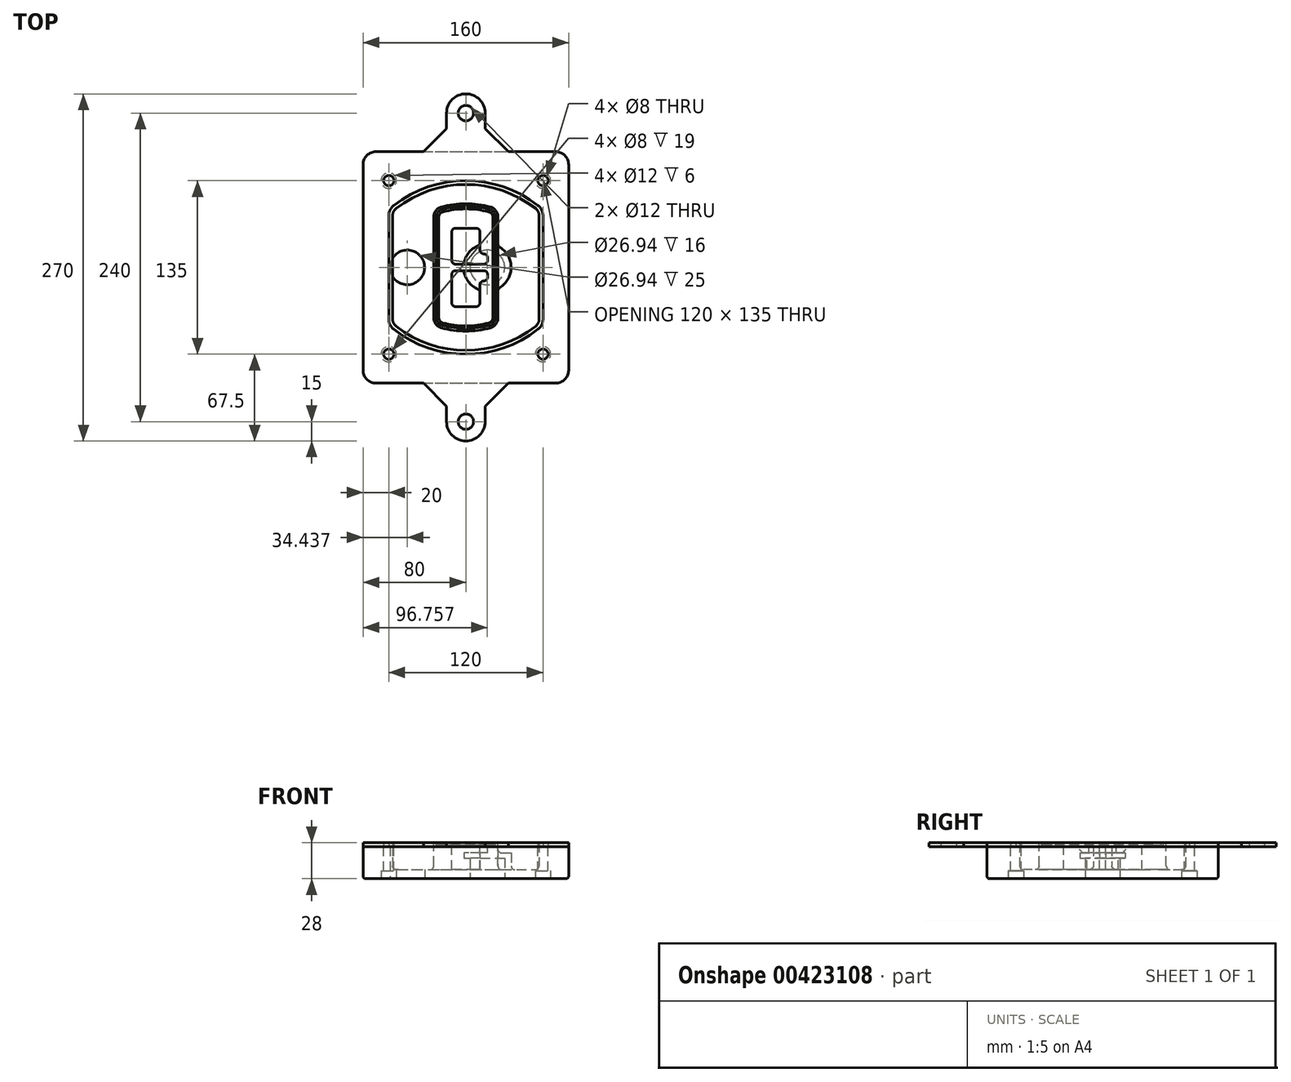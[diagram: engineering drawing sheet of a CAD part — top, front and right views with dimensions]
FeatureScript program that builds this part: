
annotation { "Feature Type Name" : "Feature", "Feature Type Description" : "" }
export const myFeature = defineFeature(function(context is Context, id is Id, definition is map)
    precondition{}
    {
        {
            var Q0;
            Q0=qCreatedBy(makeId("Top.planeOp"),FACE);
            var sketch = newSketch(context, id + "F0", { "sketchPlane" : qUnion([Q0])});
            skPoint(sketch, "E0.rect.middle", {"position": v(0, 0) * mm});
            skLineSegment(sketch, "E1.bottom", {"start": v(-70, -90) * mm, "end": v(70, -90) * mm});
            skLineSegment(sketch, "E1.top", {"start": v(-70, 90) * mm, "end": v(70, 90) * mm});
            skLineSegment(sketch, "E1.left", {"start": v(-80, -80) * mm, "end": v(-80, 80) * mm});
            skLineSegment(sketch, "E1.right", {"start": v(80, -80) * mm, "end": v(80, 80) * mm});
            skLineSegment(sketch, "E2", {"start": v(-80, 90) * mm, "end": v(80, -90) * mm, "construction": true});
            skLineSegment(sketch, "E3", {"start": v(80, 90) * mm, "end": v(-80, -90) * mm, "construction": true});
            skCircle(sketch, "E4", {"center": v(-60, 67.5) * mm, "radius": 4 * mm});
            skCircle(sketch, "E5", {"center": v(60, 67.5) * mm, "radius": 4 * mm});
            skCircle(sketch, "E6", {"center": v(60, -67.5) * mm, "radius": 4 * mm});
            skCircle(sketch, "E7", {"center": v(-60, -67.5) * mm, "radius": 4 * mm});
            skLineSegment(sketch, "E8", {"start": v(-60, 67.5) * mm, "end": v(60, 67.5) * mm, "construction": true});
            skLineSegment(sketch, "E9", {"start": v(60, 67.5) * mm, "end": v(60, -67.5) * mm, "construction": true});
            skLineSegment(sketch, "E10", {"start": v(60, -67.5) * mm, "end": v(-60, -67.5) * mm, "construction": true});
            skLineSegment(sketch, "E11", {"start": v(-60, -67.5) * mm, "end": v(-60, 67.5) * mm, "construction": true});
            skLineSegment(sketch, "E12", {"start": v(-60, 40.3) * mm, "end": v(-60, -40.3) * mm});
            skLineSegment(sketch, "E13", {"start": v(60, 40.3) * mm, "end": v(60, -40.3) * mm});
            skArc(sketch, "E14", {"start": v(56.15, 48.18) * mm, "mid": v(0, 67.5) * mm, "end": v(-56.15, 48.18) * mm});
            skArc(sketch, "E15", {"start": v(-56.15, -48.18) * mm, "mid": v(0, -67.5) * mm, "end": v(56.15, -48.18) * mm});
            skLineSegment(sketch, "E16", {"start": v(-60, 0) * mm, "end": v(60, 0) * mm, "construction": true});
            skPoint(sketch, "E17.visualSharp", {"position": v(-60, -45) * mm});
            skArc(sketch, "E17.filletArc", {"start": v(-60, -40.3) * mm, "mid": v(-58.99, -44.68) * mm, "end": v(-56.15, -48.18) * mm});
            skPoint(sketch, "E18.visualSharp", {"position": v(-60, 45) * mm});
            skArc(sketch, "E18.filletArc", {"start": v(-56.15, 48.18) * mm, "mid": v(-58.99, 44.68) * mm, "end": v(-60, 40.3) * mm});
            skPoint(sketch, "E19.visualSharp", {"position": v(60, 45) * mm});
            skArc(sketch, "E19.filletArc", {"start": v(60, 40.3) * mm, "mid": v(58.99, 44.68) * mm, "end": v(56.15, 48.18) * mm});
            skPoint(sketch, "E20.visualSharp", {"position": v(60, -45) * mm});
            skArc(sketch, "E20.filletArc", {"start": v(56.15, -48.18) * mm, "mid": v(58.99, -44.68) * mm, "end": v(60, -40.3) * mm});
            skPoint(sketch, "E21.visualSharp", {"position": v(-80, 90) * mm});
            skArc(sketch, "E21.filletArc", {"start": v(-70, 90) * mm, "mid": v(-77.07, 87.07) * mm, "end": v(-80, 80) * mm});
            skPoint(sketch, "E22.visualSharp", {"position": v(80, 90) * mm});
            skArc(sketch, "E22.filletArc", {"start": v(80, 80) * mm, "mid": v(77.07, 87.07) * mm, "end": v(70, 90) * mm});
            skPoint(sketch, "E23.visualSharp", {"position": v(80, -90) * mm});
            skArc(sketch, "E23.filletArc", {"start": v(70, -90) * mm, "mid": v(77.07, -87.07) * mm, "end": v(80, -80) * mm});
            skPoint(sketch, "E24.visualSharp", {"position": v(-80, -90) * mm});
            skArc(sketch, "E24.filletArc", {"start": v(-80, -80) * mm, "mid": v(-77.07, -87.07) * mm, "end": v(-70, -90) * mm});
            skArc(sketch, "E25.0", {"start": v(57, 40.3) * mm, "mid": v(56.3, 43.36) * mm, "end": v(54.3, 45.81) * mm});
            skLineSegment(sketch, "E25.1", {"start": v(57, 40.3) * mm, "end": v(57, -40.3) * mm});
            skArc(sketch, "E25.2", {"start": v(54.3, -45.81) * mm, "mid": v(56.3, -43.36) * mm, "end": v(57, -40.3) * mm});
            skArc(sketch, "E25.3", {"start": v(-54.3, -45.81) * mm, "mid": v(0, -64.5) * mm, "end": v(54.3, -45.81) * mm});
            skArc(sketch, "E25.4", {"start": v(-57, -40.3) * mm, "mid": v(-56.3, -43.36) * mm, "end": v(-54.3, -45.81) * mm});
            skArc(sketch, "E25.5", {"start": v(54.3, 45.81) * mm, "mid": v(0, 64.5) * mm, "end": v(-54.3, 45.81) * mm});
            skLineSegment(sketch, "E25.6", {"start": v(-57, 40.3) * mm, "end": v(-57, -40.3) * mm});
            skArc(sketch, "E25.7", {"start": v(-54.3, 45.81) * mm, "mid": v(-56.3, 43.36) * mm, "end": v(-57, 40.3) * mm});
            skArc(sketch, "E26.0", {"start": v(-58.62, 51.33) * mm, "mid": v(-62.58, 46.43) * mm, "end": v(-64, 40.3) * mm});
            skArc(sketch, "E26.1", {"start": v(58.62, 51.33) * mm, "mid": v(0, 71.5) * mm, "end": v(-58.62, 51.33) * mm});
            skArc(sketch, "E26.2", {"start": v(64, 40.3) * mm, "mid": v(62.58, 46.43) * mm, "end": v(58.62, 51.33) * mm});
            skLineSegment(sketch, "E26.3", {"start": v(64, 40.3) * mm, "end": v(64, -40.3) * mm});
            skArc(sketch, "E26.4", {"start": v(58.62, -51.33) * mm, "mid": v(62.58, -46.43) * mm, "end": v(64, -40.3) * mm});
            skLineSegment(sketch, "E26.5", {"start": v(-64, 40.3) * mm, "end": v(-64, -40.3) * mm});
            skArc(sketch, "E26.6", {"start": v(-58.62, -51.33) * mm, "mid": v(0, -71.5) * mm, "end": v(58.62, -51.33) * mm});
            skArc(sketch, "E26.7", {"start": v(-64, -40.3) * mm, "mid": v(-62.58, -46.43) * mm, "end": v(-58.62, -51.33) * mm});
            skSolve(sketch);
        }
        {
            var Q0;
            Q0=makeQuery(id+"F0.imprint","IMPRINT",FACE,{"disambiguationData":[TD([[makeQuery(id+"F0.imprint","IMPRINT",EDGE,{"derivedFrom":sQuery(id+"F0.wireOp",EDGE,"E1.bottom")}),1.0]])]});
            var Q1;
            Q1=makeQuery(id+"F0.imprint","IMPRINT",FACE,{"disambiguationData":[TD([[makeQuery(id+"F0.imprint","IMPRINT",EDGE,{"derivedFrom":sQuery(id+"F0.wireOp",EDGE,"E12")}),1.0]])]});
            var Q2;
            Q2=makeQuery(id+"F0.imprint","IMPRINT",FACE,{"disambiguationData":[TD([[makeQuery(id+"F0.imprint","IMPRINT",EDGE,{"derivedFrom":sQuery(id+"F0.wireOp",EDGE,"E25.0")}),1.0]])]});
            var Q3;
            Q3=makeQuery(id+"F0.imprint","IMPRINT",FACE,{"disambiguationData":[TD([[makeQuery(id+"F0.imprint","IMPRINT",EDGE,{"derivedFrom":sQuery(id+"F0.wireOp",EDGE,"E12")}),-1.0]])]});
            extrude(context, id + "F1", {"entities" : qUnion([Q0, Q1, Q2, Q3]), "oppositeDirection" : true, "depth" : 25 * mm});
        }
        {
            var Q0;
            Q0=makeQuery(id+"F0.imprint","IMPRINT",FACE,{"disambiguationData":[TD([[makeQuery(id+"F0.imprint","IMPRINT",EDGE,{"derivedFrom":sQuery(id+"F0.wireOp",EDGE,"E12")}),1.0]])]});
            extrude(context, id + "F2", {"entities" : qUnion([Q0]), "operationType" : NewBodyOperationType.ADD, "depth" : 3 * mm});
        }
        {
            var Q0;
            Q0=makeQuery(id+"F0.imprint","IMPRINT",FACE,{"disambiguationData":[TD([[makeQuery(id+"F0.imprint","IMPRINT",EDGE,{"derivedFrom":sQuery(id+"F0.wireOp",EDGE,"E25.0")}),1.0]])]});
            extrude(context, id + "F3", {"entities" : qUnion([Q0]), "operationType" : NewBodyOperationType.REMOVE, "oppositeDirection" : true, "depth" : 18 * mm});
        }
        {
            var Q0;
            Q0=makeQuery(id+"F2.opExtrude","CAP_FACE",FACE,{"disambiguationData":[OSD([sQuery(id+"F0.wireOp",EDGE,"E12"),sQuery(id+"F0.wireOp",EDGE,"E13"),sQuery(id+"F0.wireOp",EDGE,"E14"),sQuery(id+"F0.wireOp",EDGE,"E15"),sQuery(id+"F0.wireOp",EDGE,"E17.filletArc"),sQuery(id+"F0.wireOp",EDGE,"E18.filletArc"),sQuery(id+"F0.wireOp",EDGE,"E19.filletArc"),sQuery(id+"F0.wireOp",EDGE,"E20.filletArc"),sQuery(id+"F0.wireOp",EDGE,"E25.0"),sQuery(id+"F0.wireOp",EDGE,"E25.1"),sQuery(id+"F0.wireOp",EDGE,"E25.2"),sQuery(id+"F0.wireOp",EDGE,"E25.3"),sQuery(id+"F0.wireOp",EDGE,"E25.4"),sQuery(id+"F0.wireOp",EDGE,"E25.5"),sQuery(id+"F0.wireOp",EDGE,"E25.6"),sQuery(id+"F0.wireOp",EDGE,"E25.7")])],"isStart":false});
            var sketch = newSketch(context, id + "F4", { "sketchPlane" : qUnion([Q0])});
            skArc(sketch, "E27.0", {"start": v(-19.08, -46.97) * mm, "mid": v(0, -49.5) * mm, "end": v(19.08, -46.97) * mm});
            skArc(sketch, "E28.0", {"start": v(19.08, 46.97) * mm, "mid": v(0, 49.5) * mm, "end": v(-19.08, 46.97) * mm});
            skLineSegment(sketch, "E29", {"start": v(-25, 39.25) * mm, "end": v(-25, -39.25) * mm});
            skLineSegment(sketch, "E30", {"start": v(25, 39.25) * mm, "end": v(25, -39.25) * mm});
            skLineSegment(sketch, "E31", {"start": v(-25, 45.1) * mm, "end": v(25, 45.1) * mm, "construction": true});
            skLineSegment(sketch, "E32", {"start": v(-25, -45.1) * mm, "end": v(25, -45.1) * mm, "construction": true});
            skPoint(sketch, "E33.visualSharp", {"position": v(-25, 45.1) * mm});
            skArc(sketch, "E33.filletArc", {"start": v(-19.08, 46.97) * mm, "mid": v(-23.35, 44.11) * mm, "end": v(-25, 39.25) * mm});
            skPoint(sketch, "E34.visualSharp", {"position": v(25, 45.1) * mm});
            skArc(sketch, "E34.filletArc", {"start": v(25, 39.25) * mm, "mid": v(23.35, 44.11) * mm, "end": v(19.08, 46.97) * mm});
            skPoint(sketch, "E35.visualSharp", {"position": v(25, -45.1) * mm});
            skArc(sketch, "E35.filletArc", {"start": v(19.08, -46.97) * mm, "mid": v(23.35, -44.11) * mm, "end": v(25, -39.25) * mm});
            skPoint(sketch, "E36.visualSharp", {"position": v(-25, -45.1) * mm});
            skArc(sketch, "E36.filletArc", {"start": v(-25, -39.25) * mm, "mid": v(-23.35, -44.11) * mm, "end": v(-19.08, -46.97) * mm});
            skArc(sketch, "E37.0", {"start": v(54.3, 45.81) * mm, "mid": v(0, 64.5) * mm, "end": v(-54.3, 45.81) * mm});
            skArc(sketch, "E37.1", {"start": v(-54.3, 45.81) * mm, "mid": v(-56.3, 43.36) * mm, "end": v(-57, 40.3) * mm});
            skLineSegment(sketch, "E37.2", {"start": v(-57, 40.3) * mm, "end": v(-57, -40.3) * mm});
            skArc(sketch, "E37.3", {"start": v(-57, -40.3) * mm, "mid": v(-56.3, -43.36) * mm, "end": v(-54.3, -45.81) * mm});
            skArc(sketch, "E37.4", {"start": v(-54.3, -45.81) * mm, "mid": v(0, -64.5) * mm, "end": v(54.3, -45.81) * mm});
            skArc(sketch, "E37.5", {"start": v(54.3, -45.81) * mm, "mid": v(56.3, -43.36) * mm, "end": v(57, -40.3) * mm});
            skLineSegment(sketch, "E37.6", {"start": v(57, 40.3) * mm, "end": v(57, -40.3) * mm});
            skArc(sketch, "E37.7", {"start": v(57, 40.3) * mm, "mid": v(56.3, 43.36) * mm, "end": v(54.3, 45.81) * mm});
            skLineSegment(sketch, "E38.0", {"start": v(23, 39.25) * mm, "end": v(23, -39.25) * mm});
            skArc(sketch, "E38.1", {"start": v(18.56, -45.04) * mm, "mid": v(21.76, -42.9) * mm, "end": v(23, -39.25) * mm});
            skArc(sketch, "E38.2", {"start": v(-18.56, -45.04) * mm, "mid": v(0, -47.5) * mm, "end": v(18.56, -45.04) * mm});
            skArc(sketch, "E38.3", {"start": v(-23, -39.25) * mm, "mid": v(-21.76, -42.9) * mm, "end": v(-18.56, -45.04) * mm});
            skLineSegment(sketch, "E38.4", {"start": v(-23, 39.25) * mm, "end": v(-23, -39.25) * mm});
            skArc(sketch, "E38.5", {"start": v(23, 39.25) * mm, "mid": v(21.76, 42.9) * mm, "end": v(18.56, 45.04) * mm});
            skArc(sketch, "E38.6", {"start": v(-18.56, 45.04) * mm, "mid": v(-21.76, 42.9) * mm, "end": v(-23, 39.25) * mm});
            skArc(sketch, "E38.7", {"start": v(18.56, 45.04) * mm, "mid": v(0, 47.5) * mm, "end": v(-18.56, 45.04) * mm});
            skArc(sketch, "E39.0", {"start": v(21, 39.25) * mm, "mid": v(20.18, 41.68) * mm, "end": v(18.04, 43.1) * mm});
            skLineSegment(sketch, "E39.1", {"start": v(21, 39.25) * mm, "end": v(21, -39.25) * mm});
            skArc(sketch, "E39.2", {"start": v(18.04, -43.1) * mm, "mid": v(20.18, -41.68) * mm, "end": v(21, -39.25) * mm});
            skArc(sketch, "E39.3", {"start": v(-18.04, -43.1) * mm, "mid": v(0, -45.5) * mm, "end": v(18.04, -43.1) * mm});
            skArc(sketch, "E39.4", {"start": v(-21, -39.25) * mm, "mid": v(-20.18, -41.68) * mm, "end": v(-18.04, -43.1) * mm});
            skArc(sketch, "E39.5", {"start": v(18.04, 43.1) * mm, "mid": v(0, 45.5) * mm, "end": v(-18.04, 43.1) * mm});
            skLineSegment(sketch, "E39.6", {"start": v(-21, 39.25) * mm, "end": v(-21, -39.25) * mm});
            skArc(sketch, "E39.7", {"start": v(-18.04, 43.1) * mm, "mid": v(-20.18, 41.68) * mm, "end": v(-21, 39.25) * mm});
            skLineSegment(sketch, "E40", {"start": v(-25, 0) * mm, "end": v(25, 0) * mm, "construction": true});
            skLineSegment(sketch, "E41", {"start": v(-11, 5.5) * mm, "end": v(-11, 27.5) * mm});
            skLineSegment(sketch, "E42", {"start": v(-8, 30.5) * mm, "end": v(8, 30.5) * mm});
            skLineSegment(sketch, "E43", {"start": v(11, 27.5) * mm, "end": v(11, 13.5) * mm});
            skLineSegment(sketch, "E44", {"start": v(14, 10.5) * mm, "end": v(14, 10.5) * mm});
            skLineSegment(sketch, "E45", {"start": v(17, 7.5) * mm, "end": v(17, 5.5) * mm});
            skLineSegment(sketch, "E46", {"start": v(14, 2.5) * mm, "end": v(-8, 2.5) * mm});
            skPoint(sketch, "E47.visualSharp", {"position": v(-11, 30.5) * mm});
            skArc(sketch, "E47.filletArc", {"start": v(-8, 30.5) * mm, "mid": v(-10.12, 29.62) * mm, "end": v(-11, 27.5) * mm});
            skPoint(sketch, "E48.visualSharp", {"position": v(11, 30.5) * mm});
            skArc(sketch, "E48.filletArc", {"start": v(11, 27.5) * mm, "mid": v(10.12, 29.62) * mm, "end": v(8, 30.5) * mm});
            skPoint(sketch, "E49.visualSharp", {"position": v(11, 10.5) * mm});
            skArc(sketch, "E49.filletArc", {"start": v(11, 13.5) * mm, "mid": v(11.88, 11.38) * mm, "end": v(14, 10.5) * mm});
            skPoint(sketch, "E50.visualSharp", {"position": v(17, 10.5) * mm});
            skArc(sketch, "E50.filletArc", {"start": v(17, 7.5) * mm, "mid": v(16.12, 9.62) * mm, "end": v(14, 10.5) * mm});
            skPoint(sketch, "E51.visualSharp", {"position": v(17, 2.5) * mm});
            skArc(sketch, "E51.filletArc", {"start": v(14, 2.5) * mm, "mid": v(16.12, 3.38) * mm, "end": v(17, 5.5) * mm});
            skPoint(sketch, "E52.visualSharp", {"position": v(-11, 2.5) * mm});
            skArc(sketch, "E52.filletArc", {"start": v(-11, 5.5) * mm, "mid": v(-10.12, 3.38) * mm, "end": v(-8, 2.5) * mm});
            skLineSegment(sketch, "E53.0.MirrorCS", {"start": v(14, -2.5) * mm, "end": v(-8, -2.5) * mm});
            skArc(sketch, "E54.0.MirrorCS", {"start": v(-11, -5.5) * mm, "mid": v(-10.12, -3.38) * mm, "end": v(-8, -2.5) * mm});
            skLineSegment(sketch, "E55.0.MirrorCS", {"start": v(-11, -5.5) * mm, "end": v(-11, -27.5) * mm});
            skArc(sketch, "E56.0.MirrorCS", {"start": v(-8, -30.5) * mm, "mid": v(-10.12, -29.62) * mm, "end": v(-11, -27.5) * mm});
            skLineSegment(sketch, "E57.0.MirrorCS", {"start": v(-8, -30.5) * mm, "end": v(8, -30.5) * mm});
            skArc(sketch, "E58.0.MirrorCS", {"start": v(11, -27.5) * mm, "mid": v(10.12, -29.62) * mm, "end": v(8, -30.5) * mm});
            skLineSegment(sketch, "E59.0.MirrorCS", {"start": v(11, -27.5) * mm, "end": v(11, -13.5) * mm});
            skArc(sketch, "E60.0.MirrorCS", {"start": v(11, -13.5) * mm, "mid": v(11.88, -11.38) * mm, "end": v(14, -10.5) * mm});
            skArc(sketch, "E61.0.MirrorCS", {"start": v(17, -7.5) * mm, "mid": v(16.12, -9.62) * mm, "end": v(14, -10.5) * mm});
            skLineSegment(sketch, "E62.0.MirrorCS", {"start": v(17, -7.5) * mm, "end": v(17, -5.5) * mm});
            skArc(sketch, "E63.0.MirrorCS", {"start": v(14, -2.5) * mm, "mid": v(16.12, -3.38) * mm, "end": v(17, -5.5) * mm});
            skSolve(sketch);
        }
        {
            var Q0;
            Q0=makeQuery(id+"F4.imprint","IMPRINT",FACE,{"disambiguationData":[TD([[makeQuery(id+"F4.imprint","IMPRINT",EDGE,{"derivedFrom":sQuery(id+"F4.wireOp",EDGE,"E27.0")}),1.0]])]});
            var Q1;
            Q1=makeQuery(id+"F4.imprint","IMPRINT",FACE,{"disambiguationData":[TD([[makeQuery(id+"F4.imprint","IMPRINT",EDGE,{"derivedFrom":sQuery(id+"F4.wireOp",EDGE,"E38.0")}),-1.0]])]});
            var Q2;
            Q2=makeQuery(id+"F4.imprint","IMPRINT",FACE,{"disambiguationData":[TD([[makeQuery(id+"F4.imprint","IMPRINT",EDGE,{"derivedFrom":sQuery(id+"F4.wireOp",EDGE,"E39.0")}),1.0]])]});
            extrude(context, id + "F5", {"entities" : qUnion([Q0, Q1, Q2]), "operationType" : NewBodyOperationType.ADD, "endBound" : BoundingType.UP_TO_NEXT, "oppositeDirection" : true, "depth" : 25 * mm});
        }
        {
            var Q0;
            Q0=makeQuery(id+"F4.imprint","IMPRINT",FACE,{"disambiguationData":[TD([[makeQuery(id+"F4.imprint","IMPRINT",EDGE,{"derivedFrom":sQuery(id+"F4.wireOp",EDGE,"E38.0")}),-1.0]])]});
            extrude(context, id + "F6", {"entities" : qUnion([Q0]), "operationType" : NewBodyOperationType.REMOVE, "oppositeDirection" : true, "depth" : 2 * mm});
        }
        {
            var Q0;
            Q0=makeQuery(id+"F1.opExtrude","CAP_FACE",FACE,{"disambiguationData":[OSD([sQuery(id+"F0.wireOp",EDGE,"E1.bottom"),sQuery(id+"F0.wireOp",EDGE,"E1.top"),sQuery(id+"F0.wireOp",EDGE,"E1.left"),sQuery(id+"F0.wireOp",EDGE,"E1.right"),sQuery(id+"F0.wireOp",EDGE,"E4"),sQuery(id+"F0.wireOp",EDGE,"E5"),sQuery(id+"F0.wireOp",EDGE,"E6"),sQuery(id+"F0.wireOp",EDGE,"E7"),sQuery(id+"F0.wireOp",EDGE,"E21.filletArc"),sQuery(id+"F0.wireOp",EDGE,"E22.filletArc"),sQuery(id+"F0.wireOp",EDGE,"E23.filletArc"),sQuery(id+"F0.wireOp",EDGE,"E24.filletArc")])],"isStart":false});
            var sketch = newSketch(context, id + "F7", { "sketchPlane" : qUnion([Q0])});
            skCircle(sketch, "E64", {"center": v(16.76, 0) * mm, "radius": 13.47 * mm});
            skCircle(sketch, "E65", {"center": v(-45.56, 0) * mm, "radius": 13.47 * mm});
            skLineSegment(sketch, "E66", {"start": v(80, 0) * mm, "end": v(-80, 0) * mm});
            skCircle(sketch, "E67", {"center": v(16.76, 0) * mm, "radius": 18.47 * mm});
            skCircle(sketch, "E68", {"center": v(60, -67.5) * mm, "radius": 6 * mm});
            skCircle(sketch, "E69", {"center": v(-60, -67.5) * mm, "radius": 6 * mm});
            skCircle(sketch, "E70", {"center": v(-60, 67.5) * mm, "radius": 6 * mm});
            skCircle(sketch, "E71", {"center": v(60, 67.5) * mm, "radius": 6 * mm});
            skSolve(sketch);
        }
        {
            var Q0;
            {var subQ1=sQuery(id+"F7.wireOp",EDGE,"E66");var subQ4=sQuery(id+"F7.wireOp",EDGE,"E64");var subQ6=makeQuery(id+"F7.imprint","INTERSECT",VERTEX,{"disambiguationData":[OD(0.0)],"derivedFrom":[subQ4,subQ1]});Q0=makeQuery(id+"F7.imprint","IMPRINT",FACE,{"disambiguationData":[TD([[makeQuery(id+"F7.imprint","IMPRINT",EDGE,{"disambiguationData":[TD([[subQ6,-1.0]])],"derivedFrom":subQ4}),-1.0]])]});}
            var Q1;
            {var subQ0=sQuery(id+"F7.wireOp",EDGE,"E66");var subQ1=sQuery(id+"F7.wireOp",EDGE,"E64");var subQ3=makeQuery(id+"F7.imprint","INTERSECT",VERTEX,{"disambiguationData":[OD(0.0)],"derivedFrom":[subQ1,subQ0]});Q1=makeQuery(id+"F7.imprint","IMPRINT",FACE,{"disambiguationData":[TD([[makeQuery(id+"F7.imprint","IMPRINT",EDGE,{"disambiguationData":[TD([[subQ3,-1.0]])],"derivedFrom":subQ1}),1.0]])]});}
            var Q2;
            {var subQ0=sQuery(id+"F7.wireOp",EDGE,"E66");var subQ1=sQuery(id+"F7.wireOp",EDGE,"E64");var subQ3=makeQuery(id+"F7.imprint","INTERSECT",VERTEX,{"disambiguationData":[OD(0.0)],"derivedFrom":[subQ1,subQ0]});Q2=makeQuery(id+"F7.imprint","IMPRINT",FACE,{"disambiguationData":[TD([[makeQuery(id+"F7.imprint","IMPRINT",EDGE,{"disambiguationData":[TD([[subQ3,1.0]])],"derivedFrom":subQ1}),1.0]])]});}
            var Q3;
            {var subQ1=sQuery(id+"F7.wireOp",EDGE,"E66");var subQ4=sQuery(id+"F7.wireOp",EDGE,"E64");var subQ6=makeQuery(id+"F7.imprint","INTERSECT",VERTEX,{"disambiguationData":[OD(0.0)],"derivedFrom":[subQ4,subQ1]});Q3=makeQuery(id+"F7.imprint","IMPRINT",FACE,{"disambiguationData":[TD([[makeQuery(id+"F7.imprint","IMPRINT",EDGE,{"disambiguationData":[TD([[subQ6,1.0]])],"derivedFrom":subQ4}),-1.0]])]});}
            extrude(context, id + "F8", {"entities" : qUnion([Q0, Q1, Q2, Q3]), "operationType" : NewBodyOperationType.ADD, "oppositeDirection" : true, "depth" : 20 * mm});
        }
        {
            var Q0;
            {var subQ0=sQuery(id+"F7.wireOp",EDGE,"E66");var subQ1=sQuery(id+"F7.wireOp",EDGE,"E64");var subQ3=makeQuery(id+"F7.imprint","INTERSECT",VERTEX,{"disambiguationData":[OD(0.0)],"derivedFrom":[subQ1,subQ0]});Q0=makeQuery(id+"F7.imprint","IMPRINT",FACE,{"disambiguationData":[TD([[makeQuery(id+"F7.imprint","IMPRINT",EDGE,{"disambiguationData":[TD([[subQ3,-1.0]])],"derivedFrom":subQ1}),1.0]])]});}
            var Q1;
            {var subQ0=sQuery(id+"F7.wireOp",EDGE,"E66");var subQ1=sQuery(id+"F7.wireOp",EDGE,"E64");var subQ3=makeQuery(id+"F7.imprint","INTERSECT",VERTEX,{"disambiguationData":[OD(0.0)],"derivedFrom":[subQ1,subQ0]});Q1=makeQuery(id+"F7.imprint","IMPRINT",FACE,{"disambiguationData":[TD([[makeQuery(id+"F7.imprint","IMPRINT",EDGE,{"disambiguationData":[TD([[subQ3,1.0]])],"derivedFrom":subQ1}),1.0]])]});}
            extrude(context, id + "F9", {"entities" : qUnion([Q0, Q1]), "operationType" : NewBodyOperationType.REMOVE, "oppositeDirection" : true, "depth" : 16 * mm});
        }
        {
            var Q0;
            {var subQ0=sQuery(id+"F7.wireOp",EDGE,"E66");var subQ1=sQuery(id+"F7.wireOp",EDGE,"E65");var subQ3=makeQuery(id+"F7.imprint","INTERSECT",VERTEX,{"disambiguationData":[OD(0.0)],"derivedFrom":[subQ1,subQ0]});Q0=makeQuery(id+"F7.imprint","IMPRINT",FACE,{"disambiguationData":[TD([[makeQuery(id+"F7.imprint","IMPRINT",EDGE,{"disambiguationData":[TD([[subQ3,-1.0]])],"derivedFrom":subQ1}),1.0]])]});}
            var Q1;
            {var subQ0=sQuery(id+"F7.wireOp",EDGE,"E66");var subQ1=sQuery(id+"F7.wireOp",EDGE,"E65");var subQ3=makeQuery(id+"F7.imprint","INTERSECT",VERTEX,{"disambiguationData":[OD(0.0)],"derivedFrom":[subQ1,subQ0]});Q1=makeQuery(id+"F7.imprint","IMPRINT",FACE,{"disambiguationData":[TD([[makeQuery(id+"F7.imprint","IMPRINT",EDGE,{"disambiguationData":[TD([[subQ3,1.0]])],"derivedFrom":subQ1}),1.0]])]});}
            extrude(context, id + "F10", {"entities" : qUnion([Q0, Q1]), "operationType" : NewBodyOperationType.REMOVE, "oppositeDirection" : true, "depth" : 25 * mm});
        }
        {
            var Q0;
            Q0=makeQuery(id+"F7.imprint","IMPRINT",FACE,{"disambiguationData":[TD([[makeQuery(id+"F7.imprint","IMPRINT",EDGE,{"derivedFrom":sQuery(id+"F7.wireOp",EDGE,"E68")}),1.0]])]});
            var Q1;
            Q1=makeQuery(id+"F7.imprint","IMPRINT",FACE,{"disambiguationData":[TD([[makeQuery(id+"F7.imprint","IMPRINT",EDGE,{"derivedFrom":makeQuery(id+"F1.opExtrude","CAP_EDGE",EDGE,{"disambiguationData":[OSD([sQuery(id+"F0.wireOp",EDGE,"E5")])],"isStart":false})}),-1.0]])]});
            var Q2;
            Q2=makeQuery(id+"F7.imprint","IMPRINT",FACE,{"disambiguationData":[TD([[makeQuery(id+"F7.imprint","IMPRINT",EDGE,{"derivedFrom":sQuery(id+"F7.wireOp",EDGE,"E69")}),1.0]])]});
            var Q3;
            Q3=makeQuery(id+"F7.imprint","IMPRINT",FACE,{"disambiguationData":[TD([[makeQuery(id+"F7.imprint","IMPRINT",EDGE,{"derivedFrom":makeQuery(id+"F1.opExtrude","CAP_EDGE",EDGE,{"disambiguationData":[OSD([sQuery(id+"F0.wireOp",EDGE,"E4")])],"isStart":false})}),-1.0]])]});
            var Q4;
            Q4=makeQuery(id+"F7.imprint","IMPRINT",FACE,{"disambiguationData":[TD([[makeQuery(id+"F7.imprint","IMPRINT",EDGE,{"derivedFrom":sQuery(id+"F7.wireOp",EDGE,"E70")}),1.0]])]});
            var Q5;
            Q5=makeQuery(id+"F7.imprint","IMPRINT",FACE,{"disambiguationData":[TD([[makeQuery(id+"F7.imprint","IMPRINT",EDGE,{"derivedFrom":makeQuery(id+"F1.opExtrude","CAP_EDGE",EDGE,{"disambiguationData":[OSD([sQuery(id+"F0.wireOp",EDGE,"E7")])],"isStart":false})}),-1.0]])]});
            var Q6;
            Q6=makeQuery(id+"F7.imprint","IMPRINT",FACE,{"disambiguationData":[TD([[makeQuery(id+"F7.imprint","IMPRINT",EDGE,{"derivedFrom":sQuery(id+"F7.wireOp",EDGE,"E71")}),1.0]])]});
            var Q7;
            Q7=makeQuery(id+"F7.imprint","IMPRINT",FACE,{"disambiguationData":[TD([[makeQuery(id+"F7.imprint","IMPRINT",EDGE,{"derivedFrom":makeQuery(id+"F1.opExtrude","CAP_EDGE",EDGE,{"disambiguationData":[OSD([sQuery(id+"F0.wireOp",EDGE,"E6")])],"isStart":false})}),-1.0]])]});
            extrude(context, id + "F11", {"entities" : qUnion([Q0, Q1, Q2, Q3, Q4, Q5, Q6, Q7]), "operationType" : NewBodyOperationType.REMOVE, "oppositeDirection" : true, "depth" : 6 * mm});
        }
        {
            var Q0;
            Q0=makeQuery(id+"F9.boolean.opBoolean","COPY",FACE,{"derivedFrom":makeQuery(id+"F9.opExtrude","CAP_FACE",FACE,{"disambiguationData":[OSD([sQuery(id+"F7.wireOp",EDGE,"E64")])],"isStart":false})});
            var sketch = newSketch(context, id + "F12", { "sketchPlane" : qUnion([Q0])});
            skArc(sketch, "E72.0", {"start": v(11, 17.55) * mm, "mid": v(2.57, 11.82) * mm, "end": v(-1.54, 2.5) * mm});
            skArc(sketch, "E72.1", {"start": v(-1.54, -2.5) * mm, "mid": v(2.57, -11.82) * mm, "end": v(11, -17.55) * mm});
            skLineSegment(sketch, "E73", {"start": v(-1.54, -2.5) * mm, "end": v(14, -2.5) * mm});
            skLineSegment(sketch, "E74.0", {"start": v(14, 2.5) * mm, "end": v(-1.54, 2.5) * mm});
            skArc(sketch, "E74.1", {"start": v(14, 2.5) * mm, "mid": v(16.12, 3.38) * mm, "end": v(17, 5.5) * mm});
            skLineSegment(sketch, "E74.2", {"start": v(17, 7.5) * mm, "end": v(17, 5.5) * mm});
            skArc(sketch, "E74.3", {"start": v(17, 7.5) * mm, "mid": v(16.12, 9.62) * mm, "end": v(14, 10.5) * mm});
            skArc(sketch, "E74.4", {"start": v(11, 13.5) * mm, "mid": v(11.88, 11.38) * mm, "end": v(14, 10.5) * mm});
            skLineSegment(sketch, "E74.5", {"start": v(11, 17.55) * mm, "end": v(11, 13.5) * mm});
            skLineSegment(sketch, "E74.7", {"start": v(14, -2.5) * mm, "end": v(-1.54, -2.5) * mm});
            skArc(sketch, "E74.8", {"start": v(14, -2.5) * mm, "mid": v(16.12, -3.38) * mm, "end": v(17, -5.5) * mm});
            skLineSegment(sketch, "E74.9", {"start": v(17, -7.5) * mm, "end": v(17, -5.5) * mm});
            skArc(sketch, "E74.10", {"start": v(17, -7.5) * mm, "mid": v(16.12, -9.62) * mm, "end": v(14, -10.5) * mm});
            skArc(sketch, "E74.11", {"start": v(11, -13.5) * mm, "mid": v(11.88, -11.38) * mm, "end": v(14, -10.5) * mm});
            skLineSegment(sketch, "E74.12", {"start": v(11, -17.55) * mm, "end": v(11, -13.5) * mm});
            skPoint(sketch, "E75.orphan", {"position": v(11, -27.5) * mm});
            skPoint(sketch, "E76.orphan", {"position": v(-8, -2.5) * mm});
            skPoint(sketch, "E77.orphan", {"position": v(-8, 2.5) * mm});
            skPoint(sketch, "E78.orphan", {"position": v(11, 27.5) * mm});
            skSolve(sketch);
        }
        {
            var Q0;
            {var subQ7=sQuery(id+"F12.wireOp",EDGE,"E72.0");var subQ14=sQuery(id+"F12.wireOp",EDGE,"E72.1");var subQ16=sQuery(id+"F12.wireOp",EDGE,"E74.1");var subQ18=sQuery(id+"F12.wireOp",EDGE,"E74.8");Q0=qUnion([makeQuery(id+"F12.imprint","IMPRINT",FACE,{"disambiguationData":[TD([[makeQuery(id+"F12.imprint","IMPRINT",EDGE,{"derivedFrom":subQ7}),1.0]])]}),makeQuery(id+"F12.imprint","IMPRINT",FACE,{"disambiguationData":[TD([[makeQuery(id+"F12.imprint","IMPRINT",EDGE,{"derivedFrom":subQ14}),1.0]])]}),makeQuery(id+"F12.imprint","IMPRINT",FACE,{"disambiguationData":[TD([[makeQuery(id+"F12.imprint","IMPRINT",EDGE,{"derivedFrom":subQ16}),1.0]])]}),makeQuery(id+"F12.imprint","IMPRINT",FACE,{"disambiguationData":[TD([[makeQuery(id+"F12.imprint","IMPRINT",EDGE,{"derivedFrom":subQ18}),-1.0]])]})]);}
            var Q1;
            Q1=makeQuery(id+"F5.boolean.opBoolean","SPLIT",FACE,{"disambiguationData":[TD([makeQuery(id+"F5.opExtrude","SWEPT_FACE",FACE,{"disambiguationData":[OSD([sQuery(id+"F4.wireOp",EDGE,"E41")])]})])],"derivedFrom":makeQuery(id+"F3.boolean.opBoolean","COPY",FACE,{"derivedFrom":makeQuery(id+"F3.opExtrude","CAP_FACE",FACE,{"disambiguationData":[OSD([sQuery(id+"F0.wireOp",EDGE,"E25.0"),sQuery(id+"F0.wireOp",EDGE,"E25.1"),sQuery(id+"F0.wireOp",EDGE,"E25.2"),sQuery(id+"F0.wireOp",EDGE,"E25.3"),sQuery(id+"F0.wireOp",EDGE,"E25.4"),sQuery(id+"F0.wireOp",EDGE,"E25.5"),sQuery(id+"F0.wireOp",EDGE,"E25.6"),sQuery(id+"F0.wireOp",EDGE,"E25.7")])],"isStart":false})})});
            extrude(context, id + "F13", {"entities" : qUnion([Q0]), "operationType" : NewBodyOperationType.REMOVE, "endBound" : BoundingType.UP_TO_SURFACE, "endBoundEntityFace" : qUnion([Q1]), "depth" : 25 * mm});
        }
        {
            var Q0;
            Q0=makeQuery(id+"F3.boolean.opBoolean","COPY",EDGE,{"derivedFrom":makeQuery(id+"F3.opExtrude","CAP_EDGE",EDGE,{"disambiguationData":[OSD([sQuery(id+"F0.wireOp",EDGE,"E25.6")])],"isStart":false})});
            var Q1;
            Q1=makeQuery(id+"F8.boolean.opBoolean","INTERSECT",EDGE,{"derivedFrom":[makeQuery(id+"F5.opExtrude","SWEPT_FACE",FACE,{"disambiguationData":[OSD([sQuery(id+"F4.wireOp",EDGE,"E30")])]}),makeQuery(id+"F8.opExtrude","CAP_FACE",FACE,{"disambiguationData":[OSD([sQuery(id+"F7.wireOp",EDGE,"E67")])],"isStart":false})]});
            var Q2;
            Q2=makeQuery(id+"F8.boolean.opBoolean","INTERSECT",EDGE,{"disambiguationData":[OD(1.0)],"derivedFrom":[makeQuery(id+"F5.opExtrude","SWEPT_FACE",FACE,{"disambiguationData":[OSD([sQuery(id+"F4.wireOp",EDGE,"E30")])]}),makeQuery(id+"F8.opExtrude","SWEPT_FACE",FACE,{"disambiguationData":[OSD([sQuery(id+"F7.wireOp",EDGE,"E67")])]})]});
            var Q3;
            {var subQ0=sQuery(id+"F4.wireOp",EDGE,"E30");Q3=makeQuery(id+"F8.boolean.opBoolean","SPLIT",EDGE,{"disambiguationData":[TD([makeQuery(id+"F5.opExtrude","SWEPT_FACE",FACE,{"disambiguationData":[OSD([sQuery(id+"F4.wireOp",EDGE,"E35.filletArc")])]})])],"derivedFrom":makeQuery(id+"F5.opExtrude","CAP_EDGE",EDGE,{"disambiguationData":[OSD([subQ0])],"isStart":false})});}
            var Q4;
            {var subQ0=sQuery(id+"F0.wireOp",EDGE,"E25.7");var subQ1=sQuery(id+"F0.wireOp",EDGE,"E25.1");var subQ2=sQuery(id+"F0.wireOp",EDGE,"E25.6");var subQ3=sQuery(id+"F0.wireOp",EDGE,"E25.5");var subQ4=sQuery(id+"F0.wireOp",EDGE,"E25.4");var subQ5=sQuery(id+"F0.wireOp",EDGE,"E25.0");var subQ6=sQuery(id+"F0.wireOp",EDGE,"E25.2");var subQ7=sQuery(id+"F0.wireOp",EDGE,"E25.3");Q4=makeQuery(id+"F8.boolean.opBoolean","INTERSECT",EDGE,{"derivedFrom":[makeQuery(id+"F5.boolean.opBoolean","SPLIT",FACE,{"disambiguationData":[TD([makeQuery(id+"F2.opExtrude","SWEPT_FACE",FACE,{"disambiguationData":[OSD([subQ5])]})])],"derivedFrom":makeQuery(id+"F3.boolean.opBoolean","COPY",FACE,{"derivedFrom":makeQuery(id+"F3.opExtrude","CAP_FACE",FACE,{"disambiguationData":[OSD([subQ5,subQ1,subQ6,subQ7,subQ4,subQ3,subQ2,subQ0])],"isStart":false})})}),makeQuery(id+"F8.opExtrude","SWEPT_FACE",FACE,{"disambiguationData":[OSD([sQuery(id+"F7.wireOp",EDGE,"E67")])]})]});}
            var Q5;
            Q5=makeQuery(id+"F8.boolean.opBoolean","INTERSECT",EDGE,{"disambiguationData":[OD(0.0)],"derivedFrom":[makeQuery(id+"F5.opExtrude","SWEPT_FACE",FACE,{"disambiguationData":[OSD([sQuery(id+"F4.wireOp",EDGE,"E30")])]}),makeQuery(id+"F8.opExtrude","SWEPT_FACE",FACE,{"disambiguationData":[OSD([sQuery(id+"F7.wireOp",EDGE,"E67")])]})]});
            fillet(context, id + "F14", {"entities" : qUnion([Q0, Q1, Q2, Q3, Q4, Q5]), "radius" : 3 * mm, "tangentPropagation" : true, "allowEdgeOverflow" : false});
        }
        {
            var Q0;
            Q0=makeQuery(id+"F1.opExtrude","CAP_EDGE",EDGE,{"disambiguationData":[OSD([sQuery(id+"F0.wireOp",EDGE,"E1.bottom")])],"isStart":false});
            fillet(context, id + "F15", {"entities" : qUnion([Q0]), "radius" : 2 * mm, "tangentPropagation" : true, "allowEdgeOverflow" : false});
        }
        {
            var Q0;
            {var subQ0=sQuery(id+"F0.wireOp",EDGE,"E21.filletArc");var subQ1=sQuery(id+"F0.wireOp",EDGE,"E7");var subQ2=sQuery(id+"F0.wireOp",EDGE,"E6");var subQ3=sQuery(id+"F0.wireOp",EDGE,"E5");var subQ4=sQuery(id+"F0.wireOp",EDGE,"E4");var subQ5=sQuery(id+"F0.wireOp",EDGE,"E22.filletArc");var subQ6=sQuery(id+"F0.wireOp",EDGE,"E1.bottom");var subQ7=sQuery(id+"F0.wireOp",EDGE,"E1.right");var subQ8=sQuery(id+"F0.wireOp",EDGE,"E1.top");var subQ9=sQuery(id+"F0.wireOp",EDGE,"E1.left");var subQ10=sQuery(id+"F0.wireOp",EDGE,"E23.filletArc");var subQ11=sQuery(id+"F0.wireOp",EDGE,"E24.filletArc");Q0=makeQuery(id+"F2.boolean.opBoolean","SPLIT",FACE,{"disambiguationData":[TD([makeQuery(id+"F1.opExtrude","SWEPT_FACE",FACE,{"disambiguationData":[OSD([subQ6])]})])],"derivedFrom":makeQuery(id+"F1.opExtrude","CAP_FACE",FACE,{"disambiguationData":[OSD([subQ6,subQ8,subQ9,subQ7,subQ4,subQ3,subQ2,subQ1,subQ0,subQ5,subQ10,subQ11])],"isStart":true})});}
            var sketch = newSketch(context, id + "F16", { "sketchPlane" : qUnion([Q0])});
            skLineSegment(sketch, "E79.0", {"start": v(-70, 90) * mm, "end": v(70, 90) * mm});
            skArc(sketch, "E79.1", {"start": v(-70, 90) * mm, "mid": v(-77.07, 87.07) * mm, "end": v(-80, 80) * mm});
            skLineSegment(sketch, "E79.2", {"start": v(-80, -80) * mm, "end": v(-80, 80) * mm});
            skArc(sketch, "E79.3", {"start": v(-80, -80) * mm, "mid": v(-77.07, -87.07) * mm, "end": v(-70, -90) * mm});
            skLineSegment(sketch, "E79.4", {"start": v(-70, -90) * mm, "end": v(70, -90) * mm});
            skArc(sketch, "E79.5", {"start": v(70, -90) * mm, "mid": v(77.07, -87.07) * mm, "end": v(80, -80) * mm});
            skLineSegment(sketch, "E79.6", {"start": v(80, -80) * mm, "end": v(80, 80) * mm});
            skArc(sketch, "E79.7", {"start": v(80, 80) * mm, "mid": v(77.07, 87.07) * mm, "end": v(70, 90) * mm});
            skCircle(sketch, "E80.0", {"center": v(-60, 67.5) * mm, "radius": 4 * mm});
            skCircle(sketch, "E80.1", {"center": v(60, 67.5) * mm, "radius": 4 * mm});
            skCircle(sketch, "E80.2", {"center": v(60, -67.5) * mm, "radius": 4 * mm});
            skCircle(sketch, "E80.3", {"center": v(-60, -67.5) * mm, "radius": 4 * mm});
            skLineSegment(sketch, "E81.0", {"start": v(-60, 40.3) * mm, "end": v(-60, -40.3) * mm});
            skArc(sketch, "E81.1", {"start": v(-56.15, 48.18) * mm, "mid": v(-58.99, 44.68) * mm, "end": v(-60, 40.3) * mm});
            skArc(sketch, "E81.2", {"start": v(56.15, 48.18) * mm, "mid": v(0, 67.5) * mm, "end": v(-56.15, 48.18) * mm});
            skArc(sketch, "E81.3", {"start": v(60, 40.3) * mm, "mid": v(58.99, 44.68) * mm, "end": v(56.15, 48.18) * mm});
            skLineSegment(sketch, "E81.4", {"start": v(60, 40.3) * mm, "end": v(60, -40.3) * mm});
            skArc(sketch, "E81.5", {"start": v(56.15, -48.18) * mm, "mid": v(58.99, -44.68) * mm, "end": v(60, -40.3) * mm});
            skArc(sketch, "E81.6", {"start": v(-56.15, -48.18) * mm, "mid": v(0, -67.5) * mm, "end": v(56.15, -48.18) * mm});
            skArc(sketch, "E81.7", {"start": v(-60, -40.3) * mm, "mid": v(-58.99, -44.68) * mm, "end": v(-56.15, -48.18) * mm});
            skLineSegment(sketch, "E82", {"start": v(0, 90) * mm, "end": v(0, 120) * mm, "construction": true});
            skCircle(sketch, "E83", {"center": v(0, 120) * mm, "radius": 6 * mm});
            skArc(sketch, "E84", {"start": v(15, 120) * mm, "mid": v(0, 135) * mm, "end": v(-15, 120) * mm});
            skLineSegment(sketch, "E85", {"start": v(-15, 120) * mm, "end": v(-15, 108) * mm});
            skLineSegment(sketch, "E86", {"start": v(15, 120) * mm, "end": v(15, 108) * mm});
            skLineSegment(sketch, "E87", {"start": v(-15, 108) * mm, "end": v(-33, 90) * mm});
            skLineSegment(sketch, "E88", {"start": v(15, 108) * mm, "end": v(33, 90) * mm});
            skLineSegment(sketch, "E89", {"start": v(-80, 0) * mm, "end": v(80, 0) * mm, "construction": true});
            skLineSegment(sketch, "E90.MirrorCS", {"start": v(15, -120) * mm, "end": v(15, -108) * mm});
            skLineSegment(sketch, "E91.MirrorCS", {"start": v(-15, -120) * mm, "end": v(-15, -108) * mm});
            skCircle(sketch, "E92.MirrorC", {"center": v(0, -120) * mm, "radius": 6 * mm});
            skArc(sketch, "E93.MirrorCS", {"start": v(15, -120) * mm, "mid": v(0, -135) * mm, "end": v(-15, -120) * mm});
            skLineSegment(sketch, "E94.MirrorCS", {"start": v(-15, -108) * mm, "end": v(-33, -90) * mm});
            skLineSegment(sketch, "E95.MirrorCS", {"start": v(15, -108) * mm, "end": v(33, -90) * mm});
            skLineSegment(sketch, "E96.MirrorCS", {"start": v(0, -90) * mm, "end": v(0, -120) * mm, "construction": true});
            skSolve(sketch);
        }
        {
            var Q0;
            Q0 = qSketchRegion(id + "F16", true);
            var Q1;
            Q1=makeQuery(id+"F2.opExtrude","CAP_FACE",FACE,{"disambiguationData":[OSD([sQuery(id+"F0.wireOp",EDGE,"E12"),sQuery(id+"F0.wireOp",EDGE,"E13"),sQuery(id+"F0.wireOp",EDGE,"E14"),sQuery(id+"F0.wireOp",EDGE,"E15"),sQuery(id+"F0.wireOp",EDGE,"E17.filletArc"),sQuery(id+"F0.wireOp",EDGE,"E18.filletArc"),sQuery(id+"F0.wireOp",EDGE,"E19.filletArc"),sQuery(id+"F0.wireOp",EDGE,"E20.filletArc"),sQuery(id+"F0.wireOp",EDGE,"E25.0"),sQuery(id+"F0.wireOp",EDGE,"E25.1"),sQuery(id+"F0.wireOp",EDGE,"E25.2"),sQuery(id+"F0.wireOp",EDGE,"E25.3"),sQuery(id+"F0.wireOp",EDGE,"E25.4"),sQuery(id+"F0.wireOp",EDGE,"E25.5"),sQuery(id+"F0.wireOp",EDGE,"E25.6"),sQuery(id+"F0.wireOp",EDGE,"E25.7")])],"isStart":false});
            extrude(context, id + "F17", {"entities" : qUnion([Q0]), "endBound" : BoundingType.UP_TO_SURFACE, "endBoundEntityFace" : qUnion([Q1]), "depth" : 25 * mm});
        }
    });
